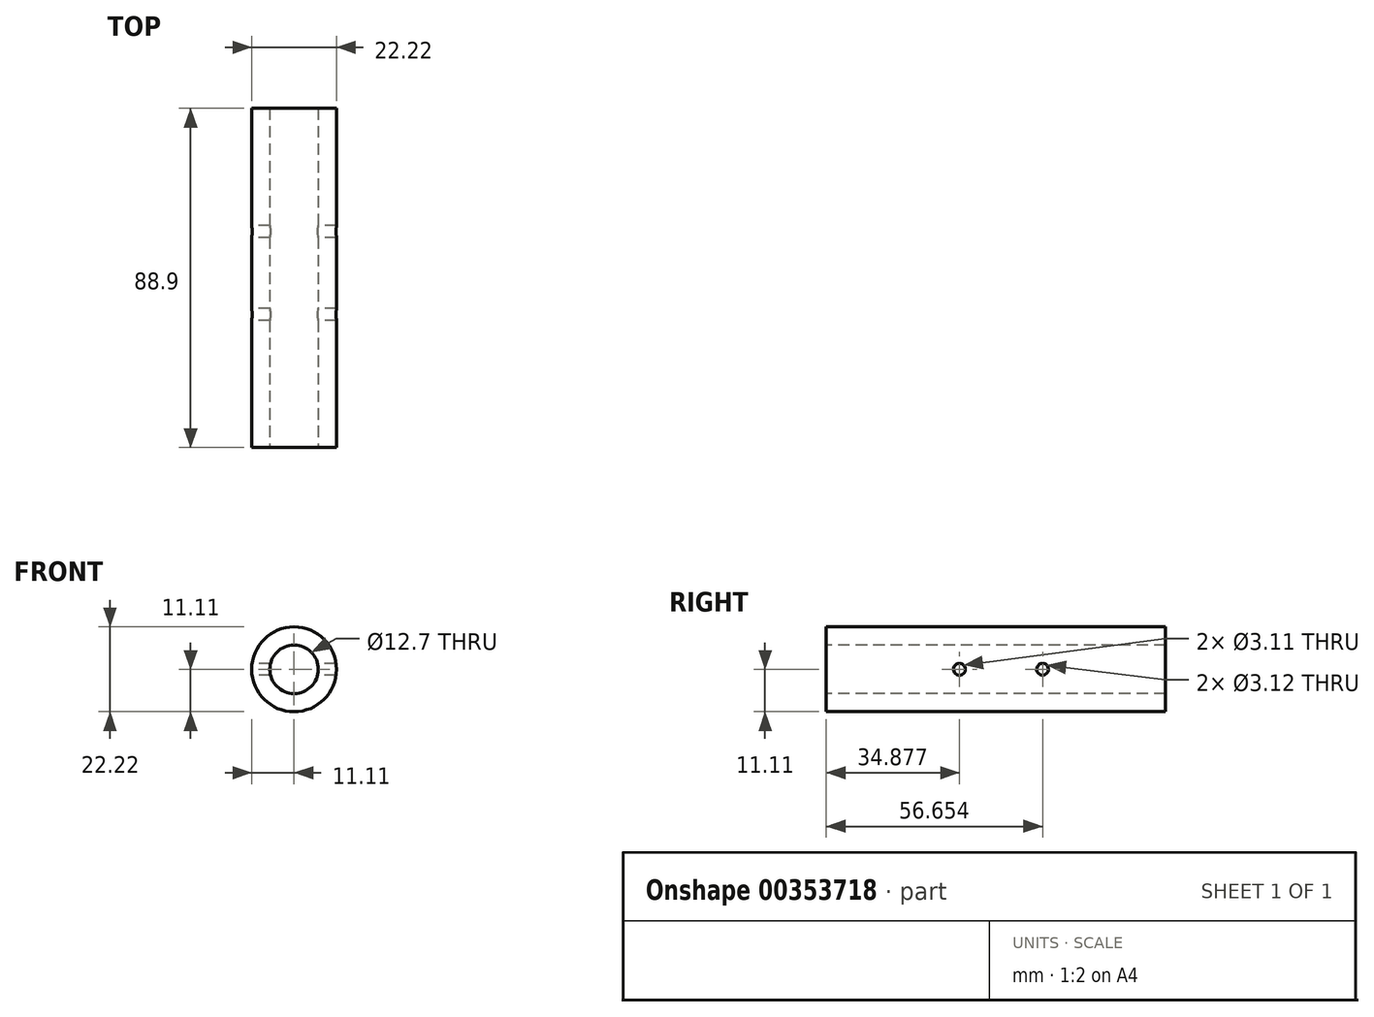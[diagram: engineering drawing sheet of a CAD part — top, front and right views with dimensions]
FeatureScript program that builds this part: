
annotation { "Feature Type Name" : "Feature", "Feature Type Description" : "" }
export const myFeature = defineFeature(function(context is Context, id is Id, definition is map)
    precondition{}
    {
        {
            var Q0;
            Q0=qCreatedBy(makeId("Front.planeOp"),FACE);
            var sketch = newSketch(context, id + "F0", { "sketchPlane" : qUnion([Q0])});
            skCircle(sketch, "E0", {"center": v(0, 0) * mm, "radius": 11.11 * mm});
            skSolve(sketch);
        }
        {
            var Q0;
            Q0 = qSketchRegion(id + "F0", true);
            extrude(context, id + "F1", {"entities" : qUnion([Q0]), "depth" : 88.9 * mm, "symmetric" : true});
        }
        {
            var Q0;
            Q0=makeQuery(id+"F1.opExtrude","CAP_FACE",FACE,{"disambiguationData":[OSD([sQuery(id+"F0.wireOp",EDGE,"E0")])],"isStart":false});
            var sketch = newSketch(context, id + "F2", { "sketchPlane" : qUnion([Q0])});
            skCircle(sketch, "E1", {"center": v(0, 0) * mm, "radius": 6.35 * mm});
            skSolve(sketch);
        }
        {
            var Q0;
            Q0 = qSketchRegion(id + "F2", true);
            extrude(context, id + "F3", {"entities" : qUnion([Q0]), "operationType" : NewBodyOperationType.REMOVE, "oppositeDirection" : true, "depth" : 88.9 * mm});
        }
        {
            var Q0;
            Q0=qCreatedBy(makeId("Right.planeOp"),FACE);
            var sketch = newSketch(context, id + "F4", { "sketchPlane" : qUnion([Q0])});
            skLineSegment(sketch, "E2", {"start": v(38.86, 0) * mm, "end": v(12.2, 0) * mm, "construction": true});
            skCircle(sketch, "E3", {"center": v(12.2, 0) * mm, "radius": 1.56 * mm});
            skLineSegment(sketch, "E4", {"start": v(12.2, 0) * mm, "end": v(10.65, 0) * mm, "construction": true});
            skCircle(sketch, "E5", {"center": v(-9.57, 0) * mm, "radius": 1.56 * mm});
            skLineSegment(sketch, "E6", {"start": v(-9.57, 0) * mm, "end": v(-38.89, 0) * mm, "construction": true});
            skLineSegment(sketch, "E7.trimOffspring", {"start": v(-8.02, 0) * mm, "end": v(-9.57, 0) * mm, "construction": true});
            skLineSegment(sketch, "E8", {"start": v(13.76, 0) * mm, "end": v(-11.13, 0) * mm, "construction": true});
            skSolve(sketch);
        }
        {
            var Q0;
            Q0 = qSketchRegion(id + "F4", true);
            extrude(context, id + "F5", {"entities" : qUnion([Q0]), "operationType" : NewBodyOperationType.REMOVE, "depth" : 25.4 * mm, "symmetric" : true});
        }
        {
            var Q0;
            Q0 = qSketchRegion(id + "F4", true);
            extrude(context, id + "F6", {"entities" : qUnion([Q0]), "operationType" : NewBodyOperationType.REMOVE, "depth" : 25.4 * mm, "symmetric" : true});
        }
    });
